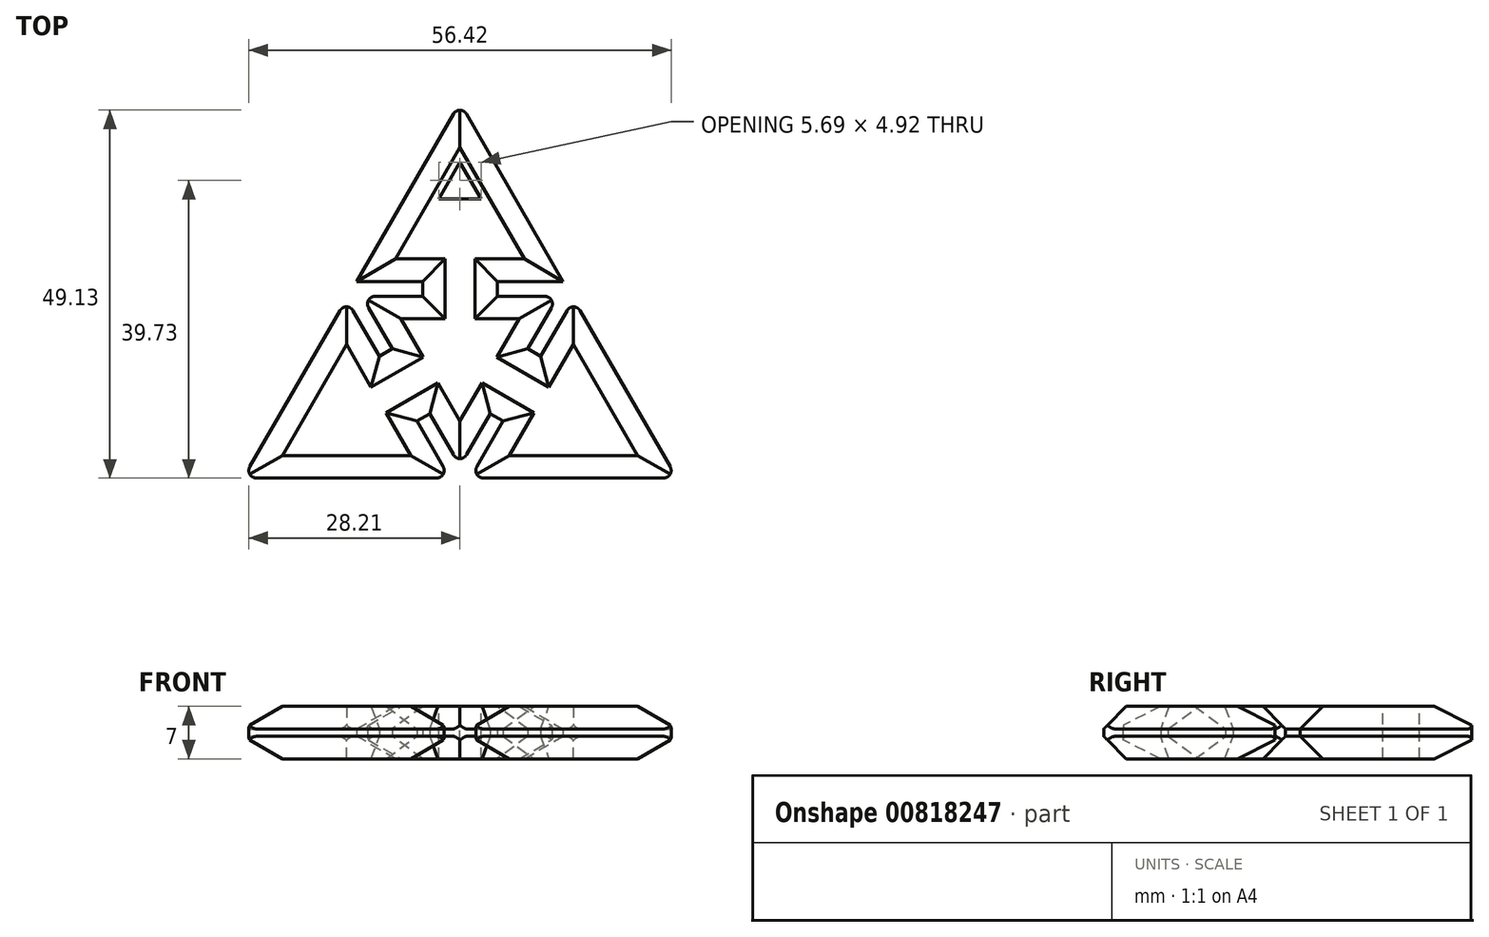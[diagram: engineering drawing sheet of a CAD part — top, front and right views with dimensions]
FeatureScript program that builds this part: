
annotation { "Feature Type Name" : "Feature", "Feature Type Description" : "" }
export const myFeature = defineFeature(function(context is Context, id is Id, definition is map)
    precondition{}
    {
        {
            var Q0;
            Q0=qCreatedBy(makeId("Top.planeOp"),FACE);
            var sketch = newSketch(context, id + "F0", { "sketchPlane" : qUnion([Q0])});
            skLineSegment(sketch, "E0.0", {"start": v(33.1, -19.1) * mm, "end": v(-33.1, -19.1) * mm});
            skLineSegment(sketch, "E0.1", {"start": v(-33.1, -19.1) * mm, "end": v(0, 38.22) * mm});
            skLineSegment(sketch, "E0.2", {"start": v(0, 38.22) * mm, "end": v(33.1, -19.1) * mm});
            skPoint(sketch, "E0.0.midPoint", {"position": v(0, -19.1) * mm});
            skLineSegment(sketch, "E1", {"start": v(0, 38.22) * mm, "end": v(0, -19.1) * mm});
            skLineSegment(sketch, "E2", {"start": v(0, -19.1) * mm, "end": v(-16.55, 9.55) * mm});
            skLineSegment(sketch, "E3", {"start": v(0, -19.1) * mm, "end": v(16.55, 9.55) * mm});
            skLineSegment(sketch, "E4", {"start": v(-16.55, 9.55) * mm, "end": v(16.55, 9.55) * mm});
            skPoint(sketch, "E0.cCircle.center.orphan", {"position": v(0, 0) * mm});
            skLineSegment(sketch, "E5.0", {"start": v(-13.08, 7.55) * mm, "end": v(13.08, 7.55) * mm});
            skLineSegment(sketch, "E5.1", {"start": v(0, -15.1) * mm, "end": v(-13.08, 7.55) * mm});
            skLineSegment(sketch, "E5.2", {"start": v(0, -15.1) * mm, "end": v(13.08, 7.55) * mm});
            skLineSegment(sketch, "E6", {"start": v(-8.27, -4.78) * mm, "end": v(-6.54, -3.78) * mm});
            skLineSegment(sketch, "E7", {"start": v(8.27, -4.78) * mm, "end": v(6.54, -3.78) * mm});
            skLineSegment(sketch, "E8", {"start": v(0, 9.55) * mm, "end": v(0, 7.55) * mm});
            skLineSegment(sketch, "E9.0", {"start": v(-6.38, -9.46) * mm, "end": v(-4.04, -8.1) * mm});
            skLineSegment(sketch, "E10.0", {"start": v(-11.38, -0.8) * mm, "end": v(-9.04, 0.55) * mm});
            skLineSegment(sketch, "E11.0", {"start": v(11.38, -0.8) * mm, "end": v(9.04, 0.55) * mm});
            skLineSegment(sketch, "E12.0", {"start": v(6.38, -9.46) * mm, "end": v(4.04, -8.1) * mm});
            skLineSegment(sketch, "E13.0", {"start": v(-5, 10.25) * mm, "end": v(-5, 7.55) * mm});
            skLineSegment(sketch, "E14.0", {"start": v(5, 10.25) * mm, "end": v(5, 7.55) * mm});
            skLineSegment(sketch, "E15.0", {"start": v(-28.94, -16.7) * mm, "end": v(0, 33.42) * mm});
            skLineSegment(sketch, "E15.1", {"start": v(28.94, -16.7) * mm, "end": v(-28.94, -16.7) * mm});
            skLineSegment(sketch, "E15.2", {"start": v(0, 33.42) * mm, "end": v(28.94, -16.7) * mm});
            skSolve(sketch);
        }
        {
            var Q0;
            {var subQ0=sQuery(id+"F0.wireOp",EDGE,"E5.1");var subQ2=sQuery(id+"F0.wireOp",EDGE,"E5.0");var subQ3=makeQuery(id+"F0.imprint","INTERSECT",VERTEX,{"derivedFrom":[subQ2,subQ0]});Q0=makeQuery(id+"F0.imprint","IMPRINT",FACE,{"disambiguationData":[TD([[makeQuery(id+"F0.imprint","IMPRINT",EDGE,{"disambiguationData":[TD([[subQ3,-1.0]])],"derivedFrom":subQ2}),-1.0]])]});}
            var Q1;
            {var subQ4=sQuery(id+"F0.wireOp",EDGE,"E5.0");var subQ5=makeQuery(id+"F0.imprint","INTERSECT",VERTEX,{"derivedFrom":[subQ4,sQuery(id+"F0.wireOp",EDGE,"E14.0")]});Q1=makeQuery(id+"F0.imprint","IMPRINT",FACE,{"disambiguationData":[TD([[makeQuery(id+"F0.imprint","IMPRINT",EDGE,{"disambiguationData":[TD([[subQ5,-1.0]])],"derivedFrom":subQ4}),-1.0]])]});}
            var Q2;
            {var subQ3=sQuery(id+"F0.wireOp",EDGE,"E6");Q2=makeQuery(id+"F0.imprint","IMPRINT",FACE,{"disambiguationData":[TD([[makeQuery(id+"F0.imprint","IMPRINT",EDGE,{"derivedFrom":subQ3}),1.0]])]});}
            var Q3;
            {var subQ0=sQuery(id+"F0.wireOp",EDGE,"E6");Q3=makeQuery(id+"F0.imprint","IMPRINT",FACE,{"disambiguationData":[TD([[makeQuery(id+"F0.imprint","IMPRINT",EDGE,{"derivedFrom":subQ0}),-1.0]])]});}
            var Q4;
            {var subQ0=sQuery(id+"F0.wireOp",EDGE,"E7");Q4=makeQuery(id+"F0.imprint","IMPRINT",FACE,{"disambiguationData":[TD([[makeQuery(id+"F0.imprint","IMPRINT",EDGE,{"derivedFrom":subQ0}),-1.0]])]});}
            var Q5;
            {var subQ0=sQuery(id+"F0.wireOp",EDGE,"E7");Q5=makeQuery(id+"F0.imprint","IMPRINT",FACE,{"disambiguationData":[TD([[makeQuery(id+"F0.imprint","IMPRINT",EDGE,{"derivedFrom":subQ0}),1.0]])]});}
            var Q6;
            {var subQ0=sQuery(id+"F0.wireOp",EDGE,"E4");var subQ1=sQuery(id+"F0.wireOp",EDGE,"E1");var subQ2=makeQuery(id+"F0.imprint","INTERSECT",VERTEX,{"derivedFrom":[subQ1,subQ0]});Q6=makeQuery(id+"F0.imprint","IMPRINT",FACE,{"disambiguationData":[TD([[makeQuery(id+"F0.imprint","IMPRINT",EDGE,{"disambiguationData":[TD([[subQ2,-1.0]])],"derivedFrom":subQ1}),1.0]])]});}
            var Q7;
            {var subQ0=sQuery(id+"F0.wireOp",EDGE,"E4");var subQ1=sQuery(id+"F0.wireOp",EDGE,"E1");var subQ2=makeQuery(id+"F0.imprint","INTERSECT",VERTEX,{"derivedFrom":[subQ1,subQ0]});Q7=makeQuery(id+"F0.imprint","IMPRINT",FACE,{"disambiguationData":[TD([[makeQuery(id+"F0.imprint","IMPRINT",EDGE,{"disambiguationData":[TD([[subQ2,-1.0]])],"derivedFrom":subQ1}),-1.0]])]});}
            var Q8;
            {var subQ0=sQuery(id+"F0.wireOp",EDGE,"E2");var subQ3=makeQuery(id+"F0.imprint","INTERSECT",VERTEX,{"derivedFrom":[subQ0,sQuery(id+"F0.wireOp",EDGE,"E10.0")]});Q8=makeQuery(id+"F0.imprint","IMPRINT",FACE,{"disambiguationData":[TD([[makeQuery(id+"F0.imprint","IMPRINT",EDGE,{"disambiguationData":[TD([[subQ3,-1.0]])],"derivedFrom":subQ0}),1.0]])]});}
            var Q9;
            {var subQ0=sQuery(id+"F0.wireOp",EDGE,"E3");var subQ4=sQuery(id+"F0.wireOp",EDGE,"E15.1");var subQ5=makeQuery(id+"F0.imprint","INTERSECT",VERTEX,{"derivedFrom":[subQ0,subQ4]});Q9=makeQuery(id+"F0.imprint","IMPRINT",FACE,{"disambiguationData":[TD([[makeQuery(id+"F0.imprint","IMPRINT",EDGE,{"disambiguationData":[TD([[subQ5,-1.0]])],"derivedFrom":subQ0}),-1.0]])]});}
            var Q10;
            {var subQ3=sQuery(id+"F0.wireOp",EDGE,"E4");var subQ5=makeQuery(id+"F0.imprint","INTERSECT",VERTEX,{"derivedFrom":[subQ3,sQuery(id+"F0.wireOp",EDGE,"E14.0")]});Q10=makeQuery(id+"F0.imprint","IMPRINT",FACE,{"disambiguationData":[TD([[makeQuery(id+"F0.imprint","IMPRINT",EDGE,{"disambiguationData":[TD([[subQ5,-1.0]])],"derivedFrom":subQ3}),1.0]])]});}
            var Q11;
            {var subQ0=sQuery(id+"F0.wireOp",EDGE,"E15.0");var subQ3=sQuery(id+"F0.wireOp",EDGE,"E4");var subQ6=makeQuery(id+"F0.imprint","INTERSECT",VERTEX,{"derivedFrom":[subQ3,subQ0]});Q11=makeQuery(id+"F0.imprint","IMPRINT",FACE,{"disambiguationData":[TD([[makeQuery(id+"F0.imprint","IMPRINT",EDGE,{"disambiguationData":[TD([[subQ6,-1.0]])],"derivedFrom":subQ3}),1.0]])]});}
            extrude(context, id + "F1", {"entities" : qUnion([Q0, Q1, Q2, Q3, Q4, Q5, Q6, Q7, Q8, Q9, Q10, Q11]), "depth" : 3.5 * mm, "offsetDistance" : 25 * mm});
        }
        {
            var Q0;
            Q0=makeQuery(id+"F1.opExtrude","CAP_FACE",FACE,{"disambiguationData":[OSD([sQuery(id+"F0.wireOp",EDGE,"E2"),sQuery(id+"F0.wireOp",EDGE,"E3"),sQuery(id+"F0.wireOp",EDGE,"E4"),sQuery(id+"F0.wireOp",EDGE,"E5.0"),sQuery(id+"F0.wireOp",EDGE,"E5.1"),sQuery(id+"F0.wireOp",EDGE,"E5.2"),sQuery(id+"F0.wireOp",EDGE,"E9.0"),sQuery(id+"F0.wireOp",EDGE,"E10.0"),sQuery(id+"F0.wireOp",EDGE,"E11.0"),sQuery(id+"F0.wireOp",EDGE,"E12.0"),sQuery(id+"F0.wireOp",EDGE,"E13.0"),sQuery(id+"F0.wireOp",EDGE,"E14.0"),sQuery(id+"F0.wireOp",EDGE,"E15.0"),sQuery(id+"F0.wireOp",EDGE,"E15.1"),sQuery(id+"F0.wireOp",EDGE,"E15.2")])],"isStart":false});
            chamfer(context, id + "F2", {"entities" : qUnion([Q0]), "width" : 3 * mm, "tangentPropagation" : true});
        }
        {
            var Q0;
            Q0=makeQuery(id+"F1.opExtrude","SWEPT_EDGE",EDGE,{"disambiguationData":[OSD([sQuery(id+"F0.wireOp",EDGE,"E15.0"),sQuery(id+"F0.wireOp",EDGE,"E15.1")])]});
            var Q1;
            Q1=makeQuery(id+"F1.opExtrude","SWEPT_EDGE",EDGE,{"disambiguationData":[OSD([sQuery(id+"F0.wireOp",EDGE,"E15.1"),sQuery(id+"F0.wireOp",EDGE,"E15.2")])]});
            var Q2;
            Q2=makeQuery(id+"F1.opExtrude","SWEPT_EDGE",EDGE,{"disambiguationData":[OSD([sQuery(id+"F0.wireOp",EDGE,"E1"),sQuery(id+"F0.wireOp",EDGE,"E15.0"),sQuery(id+"F0.wireOp",EDGE,"E15.2")])]});
            var Q3;
            Q3=makeQuery(id+"F1.opExtrude","SWEPT_EDGE",EDGE,{"disambiguationData":[OSD([sQuery(id+"F0.wireOp",EDGE,"E2"),sQuery(id+"F0.wireOp",EDGE,"E15.0")])]});
            var Q4;
            Q4=makeQuery(id+"F1.opExtrude","SWEPT_EDGE",EDGE,{"disambiguationData":[OSD([sQuery(id+"F0.wireOp",EDGE,"E3"),sQuery(id+"F0.wireOp",EDGE,"E15.2")])]});
            var Q5;
            Q5=makeQuery(id+"F1.opExtrude","SWEPT_EDGE",EDGE,{"disambiguationData":[OSD([sQuery(id+"F0.wireOp",EDGE,"E2"),sQuery(id+"F0.wireOp",EDGE,"E15.1")])]});
            var Q6;
            Q6=makeQuery(id+"F1.opExtrude","SWEPT_EDGE",EDGE,{"disambiguationData":[OSD([sQuery(id+"F0.wireOp",EDGE,"E3"),sQuery(id+"F0.wireOp",EDGE,"E15.1")])]});
            var Q7;
            Q7=makeQuery(id+"F1.opExtrude","SWEPT_EDGE",EDGE,{"disambiguationData":[OSD([sQuery(id+"F0.wireOp",EDGE,"E5.0"),sQuery(id+"F0.wireOp",EDGE,"E5.1")])]});
            var Q8;
            Q8=makeQuery(id+"F1.opExtrude","SWEPT_EDGE",EDGE,{"disambiguationData":[OSD([sQuery(id+"F0.wireOp",EDGE,"E5.0"),sQuery(id+"F0.wireOp",EDGE,"E5.2")])]});
            var Q9;
            Q9=makeQuery(id+"F1.opExtrude","SWEPT_EDGE",EDGE,{"disambiguationData":[OSD([sQuery(id+"F0.wireOp",EDGE,"E1"),sQuery(id+"F0.wireOp",EDGE,"E5.1"),sQuery(id+"F0.wireOp",EDGE,"E5.2")])]});
            fillet(context, id + "F3", {"entities" : qUnion([Q0, Q1, Q2, Q3, Q4, Q5, Q6, Q7, Q8, Q9]), "radius" : 1 * mm, "tangentPropagation" : true, "allowEdgeOverflow" : false});
        }
        {
            var Q0;
            Q0=makeQuery(id+"F1.opExtrude","SWEPT_BODY",BODY,{"disambiguationData":[OSD([sQuery(id+"F0.wireOp",EDGE,"E2"),sQuery(id+"F0.wireOp",EDGE,"E3"),sQuery(id+"F0.wireOp",EDGE,"E4"),sQuery(id+"F0.wireOp",EDGE,"E5.0"),sQuery(id+"F0.wireOp",EDGE,"E5.1"),sQuery(id+"F0.wireOp",EDGE,"E5.2"),sQuery(id+"F0.wireOp",EDGE,"E9.0"),sQuery(id+"F0.wireOp",EDGE,"E10.0"),sQuery(id+"F0.wireOp",EDGE,"E11.0"),sQuery(id+"F0.wireOp",EDGE,"E12.0"),sQuery(id+"F0.wireOp",EDGE,"E13.0"),sQuery(id+"F0.wireOp",EDGE,"E14.0"),sQuery(id+"F0.wireOp",EDGE,"E15.0"),sQuery(id+"F0.wireOp",EDGE,"E15.1"),sQuery(id+"F0.wireOp",EDGE,"E15.2")])]});
            var Q1;
            Q1=qCreatedBy(makeId("Top.planeOp"),FACE);
            mirror(context, id + "F4", {"operationType" : NewBodyOperationType.ADD, "entities" : qUnion([Q0]), "mirrorPlane" : qUnion([Q1])});
        }
        {
            var Q0;
            Q0=makeQuery(id+"F1.opExtrude","CAP_FACE",FACE,{"disambiguationData":[OSD([sQuery(id+"F0.wireOp",EDGE,"E2"),sQuery(id+"F0.wireOp",EDGE,"E3"),sQuery(id+"F0.wireOp",EDGE,"E4"),sQuery(id+"F0.wireOp",EDGE,"E5.0"),sQuery(id+"F0.wireOp",EDGE,"E5.1"),sQuery(id+"F0.wireOp",EDGE,"E5.2"),sQuery(id+"F0.wireOp",EDGE,"E9.0"),sQuery(id+"F0.wireOp",EDGE,"E10.0"),sQuery(id+"F0.wireOp",EDGE,"E11.0"),sQuery(id+"F0.wireOp",EDGE,"E12.0"),sQuery(id+"F0.wireOp",EDGE,"E13.0"),sQuery(id+"F0.wireOp",EDGE,"E14.0"),sQuery(id+"F0.wireOp",EDGE,"E15.0"),sQuery(id+"F0.wireOp",EDGE,"E15.1"),sQuery(id+"F0.wireOp",EDGE,"E15.2")])],"isStart":false});
            var sketch = newSketch(context, id + "F5", { "sketchPlane" : qUnion([Q0])});
            skCircle(sketch, "E16.cCircle", {"center": v(0, 22.2) * mm, "radius": 1.64 * mm, "construction": true});
            skLineSegment(sketch, "E16.0", {"start": v(2.84, 20.56) * mm, "end": v(-2.84, 20.56) * mm});
            skLineSegment(sketch, "E16.1", {"start": v(-2.84, 20.56) * mm, "end": v(0, 25.48) * mm});
            skLineSegment(sketch, "E16.2", {"start": v(0, 25.48) * mm, "end": v(2.84, 20.56) * mm});
            skPoint(sketch, "E16.0.midPoint", {"position": v(0, 20.56) * mm});
            skSolve(sketch);
        }
        {
            var Q0;
            Q0 = qSketchRegion(id + "F5", true);
            extrude(context, id + "F6", {"entities" : qUnion([Q0]), "operationType" : NewBodyOperationType.REMOVE, "oppositeDirection" : true, "depth" : 9.2 * mm, "offsetDistance" : 25 * mm});
        }
    });
